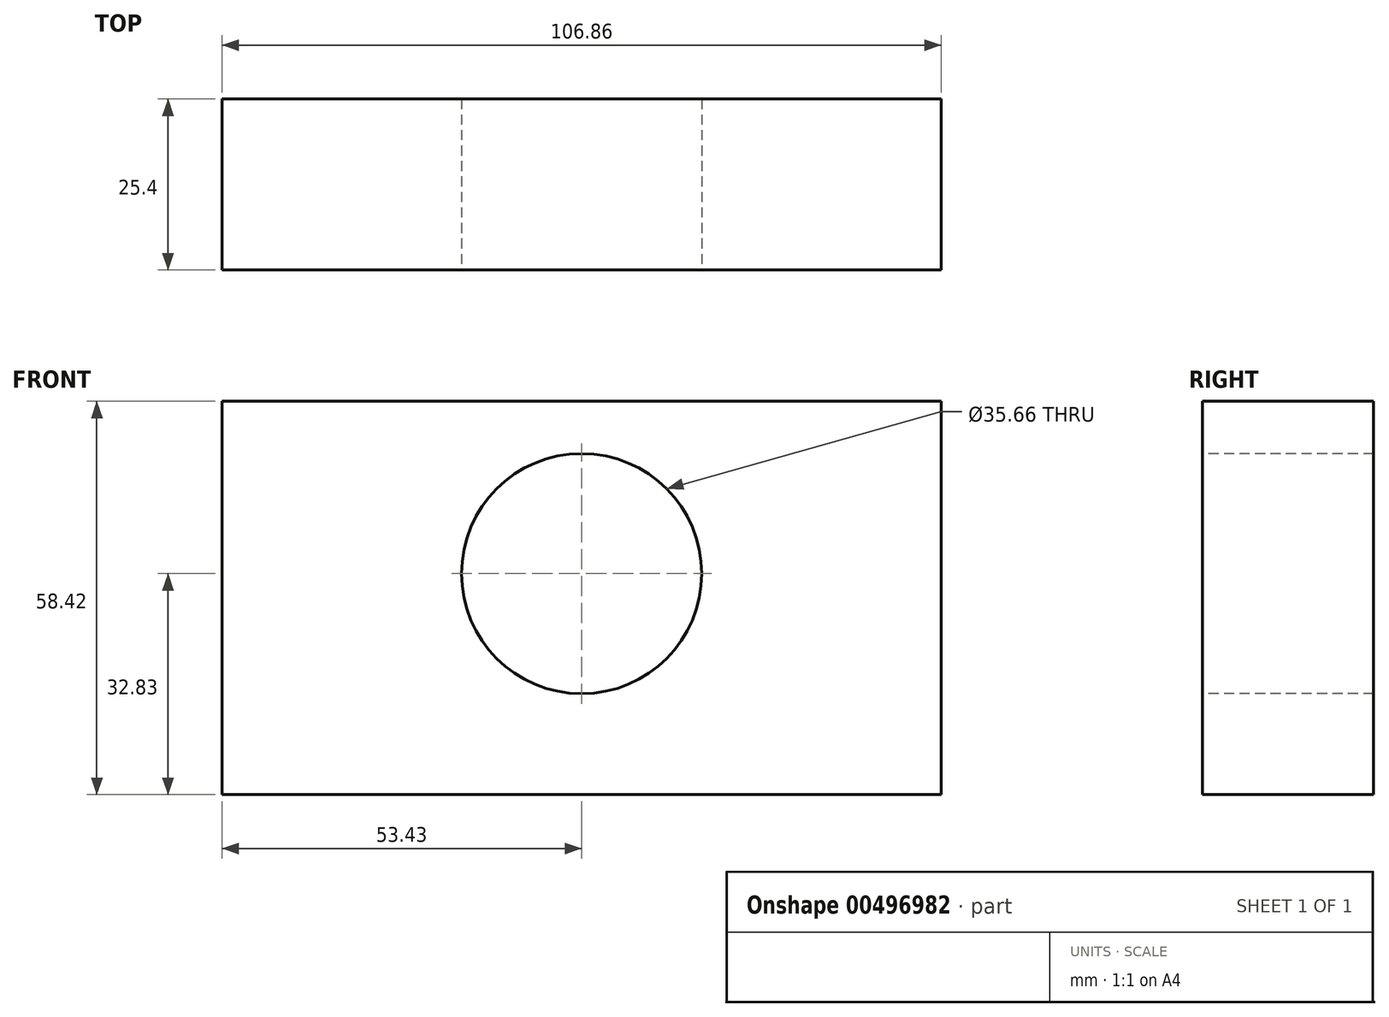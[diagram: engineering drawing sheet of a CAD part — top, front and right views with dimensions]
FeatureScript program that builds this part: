
annotation { "Feature Type Name" : "Feature", "Feature Type Description" : "" }
export const myFeature = defineFeature(function(context is Context, id is Id, definition is map)
    precondition{}
    {
        {
            var Q0;
            Q0=qCreatedBy(makeId("Front.planeOp"),FACE);
            var sketch = newSketch(context, id + "F0", { "sketchPlane" : qUnion([Q0])});
            skLineSegment(sketch, "E0.bottom", {"start": v(53.43, -32.83) * mm, "end": v(-53.43, -32.83) * mm});
            skLineSegment(sketch, "E0.top", {"start": v(53.43, 25.6) * mm, "end": v(-53.43, 25.6) * mm});
            skLineSegment(sketch, "E0.left", {"start": v(53.43, -32.83) * mm, "end": v(53.43, 25.6) * mm});
            skLineSegment(sketch, "E0.right", {"start": v(-53.43, -32.83) * mm, "end": v(-53.43, 25.6) * mm});
            skPoint(sketch, "E0.middle", {"position": v(0, -3.62) * mm});
            skCircle(sketch, "E1", {"center": v(0, 0) * mm, "radius": 17.83 * mm});
            skSolve(sketch);
        }
        {
            var Q0;
            Q0=makeQuery(id+"F0.imprint","IMPRINT",FACE,{"disambiguationData":[TD([[makeQuery(id+"F0.imprint","IMPRINT",EDGE,{"derivedFrom":sQuery(id+"F0.wireOp",EDGE,"E0.bottom")}),-1.0]])]});
            extrude(context, id + "F1", {"entities" : qUnion([Q0]), "endBound" : BoundingType.SYMMETRIC, "oppositeDirection" : true, "depth" : 25.4 * mm});
        }
    });
